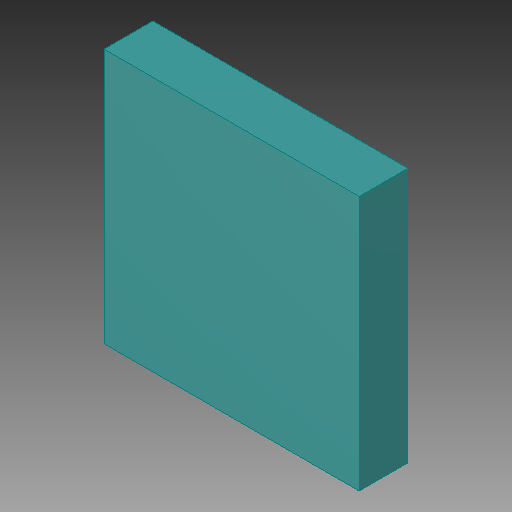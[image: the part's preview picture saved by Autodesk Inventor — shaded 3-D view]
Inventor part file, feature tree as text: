
AUTODESK INVENTOR PART (.ipt)
format: ipt  version: 2019 (Build 230136000, 136)  size: 88,576 bytes
history: native  units: in
note: dims shown in document units (in); Inventor stores cm internally (conversion verified against a paired STEP export)
features: extrude x1, other x1
ambient origin geometry x8: Origin, YZ Plane, XZ Plane, XY Plane, X Axis, Y Axis, Z Axis, Center Point
bodies: Solid1 (feature_tree)
feature tree (2):
  extrude  "Extrusion1"  Depth=0.0394in TaperAngle=0.0deg
  other  "E2_5-5, E2_5-5_3"
